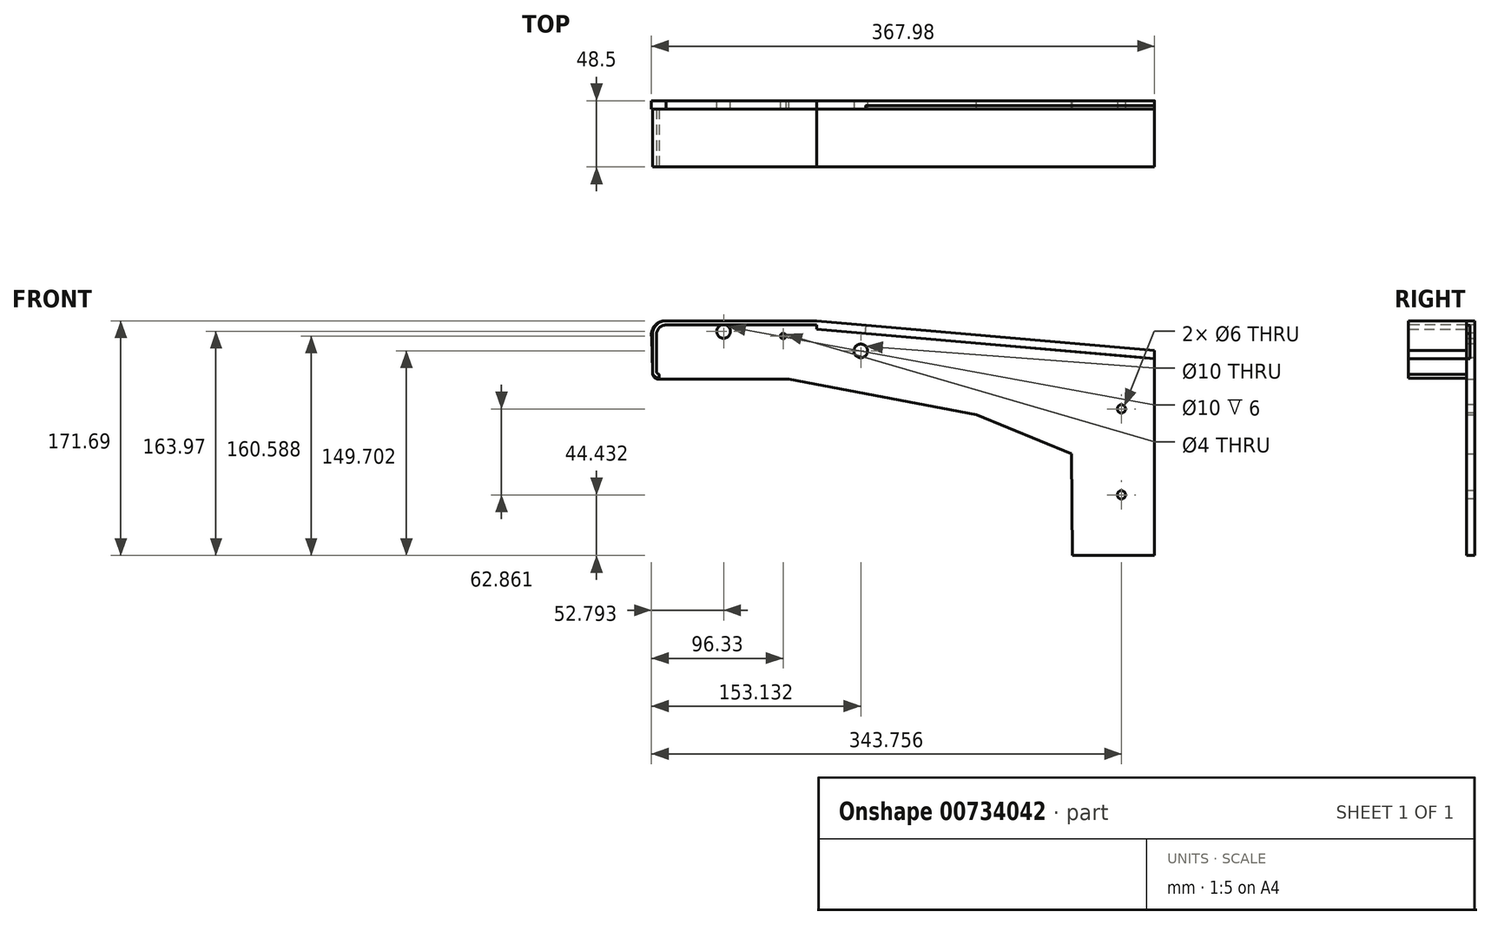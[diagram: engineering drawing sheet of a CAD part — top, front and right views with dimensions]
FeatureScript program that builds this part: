
annotation { "Feature Type Name" : "Feature", "Feature Type Description" : "" }
export const myFeature = defineFeature(function(context is Context, id is Id, definition is map)
    precondition{}
    {
        {
            var Q0;
            Q0=qCreatedBy(makeId("Front.planeOp"),FACE);
            var sketch = newSketch(context, id + "F0", { "sketchPlane" : qUnion([Q0])});
            skLineSegment(sketch, "E0", {"start": v(-49.9, 7.66) * mm, "end": v(60.1, 7.66) * mm});
            skArc(sketch, "E1", {"start": v(-49.9, 7.66) * mm, "mid": v(-58.4, 4) * mm, "end": v(-60.24, -5.07) * mm});
            skLineSegment(sketch, "E2", {"start": v(-49.93, -35) * mm, "end": v(40.07, -35) * mm});
            skLineSegment(sketch, "E3", {"start": v(307.35, -163.97) * mm, "end": v(247.35, -163.97) * mm});
            skLineSegment(sketch, "E4", {"start": v(-60.24, -5.07) * mm, "end": v(-59.88, -30.07) * mm});
            skLineSegment(sketch, "E5", {"start": v(-54.89, -35) * mm, "end": v(-49.93, -35) * mm});
            skPoint(sketch, "E6.visualSharp", {"position": v(-59.81, -35) * mm});
            skArc(sketch, "E6.filletArc", {"start": v(-59.88, -30.07) * mm, "mid": v(-58.4, -33.56) * mm, "end": v(-54.89, -35) * mm});
            skLineSegment(sketch, "E7", {"start": v(177.25, -60.95) * mm, "end": v(246.58, -89.53) * mm});
            skLineSegment(sketch, "E8", {"start": v(60.1, 7.66) * mm, "end": v(307.35, -13.97) * mm});
            skLineSegment(sketch, "E9", {"start": v(40.07, -35) * mm, "end": v(177.25, -60.95) * mm});
            skLineSegment(sketch, "E10", {"start": v(247.35, -163.97) * mm, "end": v(246.58, -89.53) * mm});
            skLineSegment(sketch, "E11", {"start": v(307.35, -163.97) * mm, "end": v(307.35, -13.97) * mm});
            skPoint(sketch, "E12.end.orphan", {"position": v(310.72, 0) * mm});
            skSolve(sketch);
        }
        {
            var Q0;
            Q0=qSketchRegion(id+"F0",true);
            extrude(context, id + "F1", {"entities" : qUnion([Q0]), "depth" : 6 * mm, "offsetDistance" : 25 * mm});
        }
        {
            var Q0;
            Q0=makeQuery(id+"F1.opExtrude","CAP_FACE",FACE,{"disambiguationData":[OSD([sQuery(id+"F0.wireOp",EDGE,"E0"),sQuery(id+"F0.wireOp",EDGE,"E1"),sQuery(id+"F0.wireOp",EDGE,"E2"),sQuery(id+"F0.wireOp",EDGE,"xIpO2BMK-1Sr3-U6kz-732z-lHFiZcdXaP95"),sQuery(id+"F0.wireOp",EDGE,"E3"),sQuery(id+"F0.wireOp",EDGE,"zyuM4KxI-rK7D-eBj5-RQWG-Z7kNhVQKbpSr"),sQuery(id+"F0.wireOp",EDGE,"E4"),sQuery(id+"F0.wireOp",EDGE,"E5"),sQuery(id+"F0.wireOp",EDGE,"E6.filletArc"),sQuery(id+"F0.wireOp",EDGE,"E7"),sQuery(id+"F0.wireOp",EDGE,"E8"),sQuery(id+"F0.wireOp",EDGE,"E9")])],"isStart":false});
            var sketch = newSketch(context, id + "F2", { "sketchPlane" : qUnion([Q0])});
            skLineSegment(sketch, "E13", {"start": v(-49.88, 0) * mm, "end": v(-60.37, 0) * mm});
            skLineSegment(sketch, "E14", {"start": v(-49.88, 0) * mm, "end": v(30.12, 0) * mm});
            skLineSegment(sketch, "E15", {"start": v(30.12, 0) * mm, "end": v(92.5, -8.77) * mm});
            skLineSegment(sketch, "E16", {"start": v(92.5, -8.77) * mm, "end": v(92.5, -14.27) * mm});
            skCircle(sketch, "E17", {"center": v(92.5, -14.27) * mm, "radius": 5 * mm});
            skSolve(sketch);
        }
        {
            var Q0;
            Q0=qSketchRegion(id+"F2",true);
            extrude(context, id + "F3", {"entities" : qUnion([Q0]), "operationType" : NewBodyOperationType.REMOVE, "endBound" : BoundingType.THROUGH_ALL, "oppositeDirection" : true, "depth" : 25 * mm, "offsetDistance" : 25 * mm});
        }
        {
            var Q0;
            Q0=makeQuery(id+"F1.opExtrude","CAP_FACE",FACE,{"disambiguationData":[OSD([sQuery(id+"F0.wireOp",EDGE,"E0"),sQuery(id+"F0.wireOp",EDGE,"E1"),sQuery(id+"F0.wireOp",EDGE,"E2"),sQuery(id+"F0.wireOp",EDGE,"xIpO2BMK-1Sr3-U6kz-732z-lHFiZcdXaP95"),sQuery(id+"F0.wireOp",EDGE,"E3"),sQuery(id+"F0.wireOp",EDGE,"zyuM4KxI-rK7D-eBj5-RQWG-Z7kNhVQKbpSr"),sQuery(id+"F0.wireOp",EDGE,"E4"),sQuery(id+"F0.wireOp",EDGE,"E5"),sQuery(id+"F0.wireOp",EDGE,"E6.filletArc"),sQuery(id+"F0.wireOp",EDGE,"E7"),sQuery(id+"F0.wireOp",EDGE,"E8"),sQuery(id+"F0.wireOp",EDGE,"E9")])],"isStart":false});
            var sketch = newSketch(context, id + "F4", { "sketchPlane" : qUnion([Q0])});
            skLineSegment(sketch, "E18", {"start": v(111.62, 3.16) * mm, "end": v(111.62, -8.84) * mm});
            skCircle(sketch, "E19", {"center": v(283.13, -119.54) * mm, "radius": 3 * mm});
            skCircle(sketch, "E20", {"center": v(283.13, -56.68) * mm, "radius": 3 * mm});
            skSolve(sketch);
        }
        {
            var Q0;
            Q0=qSketchRegion(id+"F4",true);
            extrude(context, id + "F5", {"entities" : qUnion([Q0]), "operationType" : NewBodyOperationType.REMOVE, "endBound" : BoundingType.THROUGH_ALL, "oppositeDirection" : true, "depth" : 25 * mm, "offsetDistance" : 25 * mm});
        }
        {
            var Q0;
            Q0=makeQuery(id+"F1.opExtrude","CAP_FACE",FACE,{"disambiguationData":[OSD([sQuery(id+"F0.wireOp",EDGE,"E0"),sQuery(id+"F0.wireOp",EDGE,"E1"),sQuery(id+"F0.wireOp",EDGE,"E2"),sQuery(id+"F0.wireOp",EDGE,"xIpO2BMK-1Sr3-U6kz-732z-lHFiZcdXaP95"),sQuery(id+"F0.wireOp",EDGE,"E3"),sQuery(id+"F0.wireOp",EDGE,"zyuM4KxI-rK7D-eBj5-RQWG-Z7kNhVQKbpSr"),sQuery(id+"F0.wireOp",EDGE,"E4"),sQuery(id+"F0.wireOp",EDGE,"E5"),sQuery(id+"F0.wireOp",EDGE,"E6.filletArc"),sQuery(id+"F0.wireOp",EDGE,"E7"),sQuery(id+"F0.wireOp",EDGE,"E8"),sQuery(id+"F0.wireOp",EDGE,"E9")])],"isStart":true});
            var sketch = newSketch(context, id + "F6", { "sketchPlane" : qUnion([Q0])});
            skCircle(sketch, "E21", {"center": v(7.84, 0) * mm, "radius": 5 * mm});
            skSolve(sketch);
        }
        {
            var Q0;
            Q0=qSketchRegion(id+"F6",true);
            extrude(context, id + "F7", {"entities" : qUnion([Q0]), "operationType" : NewBodyOperationType.REMOVE, "endBound" : BoundingType.THROUGH_ALL, "oppositeDirection" : true, "depth" : 25 * mm, "offsetDistance" : 25 * mm});
        }
        {
            var Q0;
            Q0=makeQuery(id+"F1.opExtrude","CAP_FACE",FACE,{"disambiguationData":[OSD([sQuery(id+"F0.wireOp",EDGE,"E0"),sQuery(id+"F0.wireOp",EDGE,"E1"),sQuery(id+"F0.wireOp",EDGE,"E2"),sQuery(id+"F0.wireOp",EDGE,"xIpO2BMK-1Sr3-U6kz-732z-lHFiZcdXaP95"),sQuery(id+"F0.wireOp",EDGE,"E3"),sQuery(id+"F0.wireOp",EDGE,"zyuM4KxI-rK7D-eBj5-RQWG-Z7kNhVQKbpSr"),sQuery(id+"F0.wireOp",EDGE,"E4"),sQuery(id+"F0.wireOp",EDGE,"E5"),sQuery(id+"F0.wireOp",EDGE,"E6.filletArc"),sQuery(id+"F0.wireOp",EDGE,"E7"),sQuery(id+"F0.wireOp",EDGE,"E8"),sQuery(id+"F0.wireOp",EDGE,"E9")])],"isStart":false});
            var sketch = newSketch(context, id + "F8", { "sketchPlane" : qUnion([Q0])});
            skCircle(sketch, "E22", {"center": v(35.7, -3.38) * mm, "radius": 2 * mm});
            skSolve(sketch);
        }
        {
            var Q0;
            Q0=qSketchRegion(id+"F8",true);
            extrude(context, id + "F9", {"entities" : qUnion([Q0]), "operationType" : NewBodyOperationType.REMOVE, "endBound" : BoundingType.THROUGH_ALL, "oppositeDirection" : true, "depth" : 25 * mm, "offsetDistance" : 25 * mm});
        }
        {
            var Q0;
            Q0=makeQuery(id+"F1.opExtrude","CAP_FACE",FACE,{"disambiguationData":[OSD([sQuery(id+"F0.wireOp",EDGE,"E0"),sQuery(id+"F0.wireOp",EDGE,"E1"),sQuery(id+"F0.wireOp",EDGE,"E2"),sQuery(id+"F0.wireOp",EDGE,"E3"),sQuery(id+"F0.wireOp",EDGE,"E4"),sQuery(id+"F0.wireOp",EDGE,"E5"),sQuery(id+"F0.wireOp",EDGE,"E6.filletArc"),sQuery(id+"F0.wireOp",EDGE,"E7"),sQuery(id+"F0.wireOp",EDGE,"E8"),sQuery(id+"F0.wireOp",EDGE,"E9"),sQuery(id+"F0.wireOp",EDGE,"E10"),sQuery(id+"F0.wireOp",EDGE,"E11")])],"isStart":false});
            var sketch = newSketch(context, id + "F10", { "sketchPlane" : qUnion([Q0])});
            skLineSegment(sketch, "E23", {"start": v(95.99, 4.53) * mm, "end": v(298.21, -13.17) * mm});
            skLineSegment(sketch, "E24", {"start": v(95.46, -1.45) * mm, "end": v(297.69, -19.14) * mm});
            skLineSegment(sketch, "E25", {"start": v(95.99, 4.53) * mm, "end": v(95.46, -1.45) * mm});
            skLineSegment(sketch, "E26", {"start": v(298.21, -13.17) * mm, "end": v(307.35, -13.97) * mm});
            skLineSegment(sketch, "E27", {"start": v(307.35, -13.97) * mm, "end": v(307.35, -19.97) * mm});
            skLineSegment(sketch, "E28", {"start": v(297.69, -19.14) * mm, "end": v(307.35, -19.97) * mm});
            skSolve(sketch);
        }
        {
            var Q0;
            Q0=qSketchRegion(id+"F10",true);
            extrude(context, id + "F11", {"entities" : qUnion([Q0]), "operationType" : NewBodyOperationType.REMOVE, "oppositeDirection" : true, "depth" : 2.5 * mm, "offsetDistance" : 25 * mm});
        }
        {
            var Q0;
            Q0=makeQuery(id+"F1.opExtrude","SWEPT_EDGE",EDGE,{"disambiguationData":[OSD([sQuery(id+"F0.wireOp",EDGE,"E8"),sQuery(id+"F0.wireOp",EDGE,"E11")])]});
            fillet(context, id + "F12", {"entities" : qUnion([Q0]), "radius" : 2 * mm, "tangentPropagation" : true, "allowEdgeOverflow" : false});
        }
        {
            var Q0;
            Q0=makeQuery(id+"F8.imprint","IMPRINT",FACE,{"disambiguationData":[TD([[makeQuery(id+"F8.imprint","IMPRINT",EDGE,{"derivedFrom":sQuery(id+"F8.wireOp",EDGE,"E22")}),-1.0]])]});
            var sketch = newSketch(context, id + "F13", { "sketchPlane" : qUnion([Q0])});
            skLineSegment(sketch, "E29", {"start": v(60.1, 1.61) * mm, "end": v(307.34, -19.95) * mm});
            skLineSegment(sketch, "E30", {"start": v(307.34, -19.95) * mm, "end": v(307.34, -13.97) * mm});
            skLineSegment(sketch, "E31", {"start": v(307.34, -13.97) * mm, "end": v(60.1, 7.72) * mm});
            skLineSegment(sketch, "E32", {"start": v(60.1, 7.72) * mm, "end": v(60.1, 1.61) * mm});
            skSolve(sketch);
        }
        {
            var Q0;
            Q0 = qSketchRegion(id + "F13", true);
            extrude(context, id + "F14", {"entities" : qUnion([Q0]), "depth" : 42.5 * mm, "offsetDistance" : 25 * mm});
        }
        {
            var Q0;
            Q0=makeQuery(id+"F14.opExtrude","CAP_FACE",FACE,{"disambiguationData":[OSD([sQuery(id+"F13.wireOp",EDGE,"E29"),sQuery(id+"F13.wireOp",EDGE,"E30"),sQuery(id+"F13.wireOp",EDGE,"E31"),sQuery(id+"F13.wireOp",EDGE,"E32")])],"isStart":false});
            var sketch = newSketch(context, id + "F15", { "sketchPlane" : qUnion([Q0])});
            skLineSegment(sketch, "E33", {"start": v(60.1, 7.72) * mm, "end": v(-49.9, 7.72) * mm});
            skLineSegment(sketch, "E34", {"start": v(-59.9, -2.28) * mm, "end": v(-59.9, -29.28) * mm});
            skPoint(sketch, "E35.visualSharp", {"position": v(-59.9, 7.72) * mm});
            skArc(sketch, "E35.filletArc", {"start": v(-49.9, 7.72) * mm, "mid": v(-56.96, 4.8) * mm, "end": v(-59.9, -2.28) * mm});
            skLineSegment(sketch, "E36", {"start": v(-54.9, -34.28) * mm, "end": v(-54.9, -34.28) * mm});
            skPoint(sketch, "E37.visualSharp", {"position": v(-59.9, -34.28) * mm});
            skArc(sketch, "E37.filletArc", {"start": v(-59.9, -29.28) * mm, "mid": v(-58.43, -32.81) * mm, "end": v(-54.9, -34.28) * mm});
            skLineSegment(sketch, "E38.0", {"start": v(60.1, 4.72) * mm, "end": v(-49.9, 4.72) * mm});
            skArc(sketch, "E39.0", {"start": v(-49.9, 4.72) * mm, "mid": v(-54.84, 2.67) * mm, "end": v(-56.9, -2.28) * mm});
            skLineSegment(sketch, "E40.0", {"start": v(-56.9, -2.28) * mm, "end": v(-56.9, -29.28) * mm});
            skArc(sketch, "E41.0", {"start": v(-56.9, -29.28) * mm, "mid": v(-56.3, -30.7) * mm, "end": v(-54.9, -31.28) * mm});
            skLineSegment(sketch, "E42", {"start": v(-54.9, -31.28) * mm, "end": v(-54.9, -34.28) * mm});
            skLineSegment(sketch, "E43", {"start": v(60.1, 7.72) * mm, "end": v(60.1, 4.72) * mm});
            skSolve(sketch);
        }
        {
            var Q0;
            Q0 = qSketchRegion(id + "F15", true);
            extrude(context, id + "F16", {"entities" : qUnion([Q0]), "operationType" : NewBodyOperationType.ADD, "oppositeDirection" : true, "depth" : 42.5 * mm, "offsetDistance" : 25 * mm});
        }
    });
